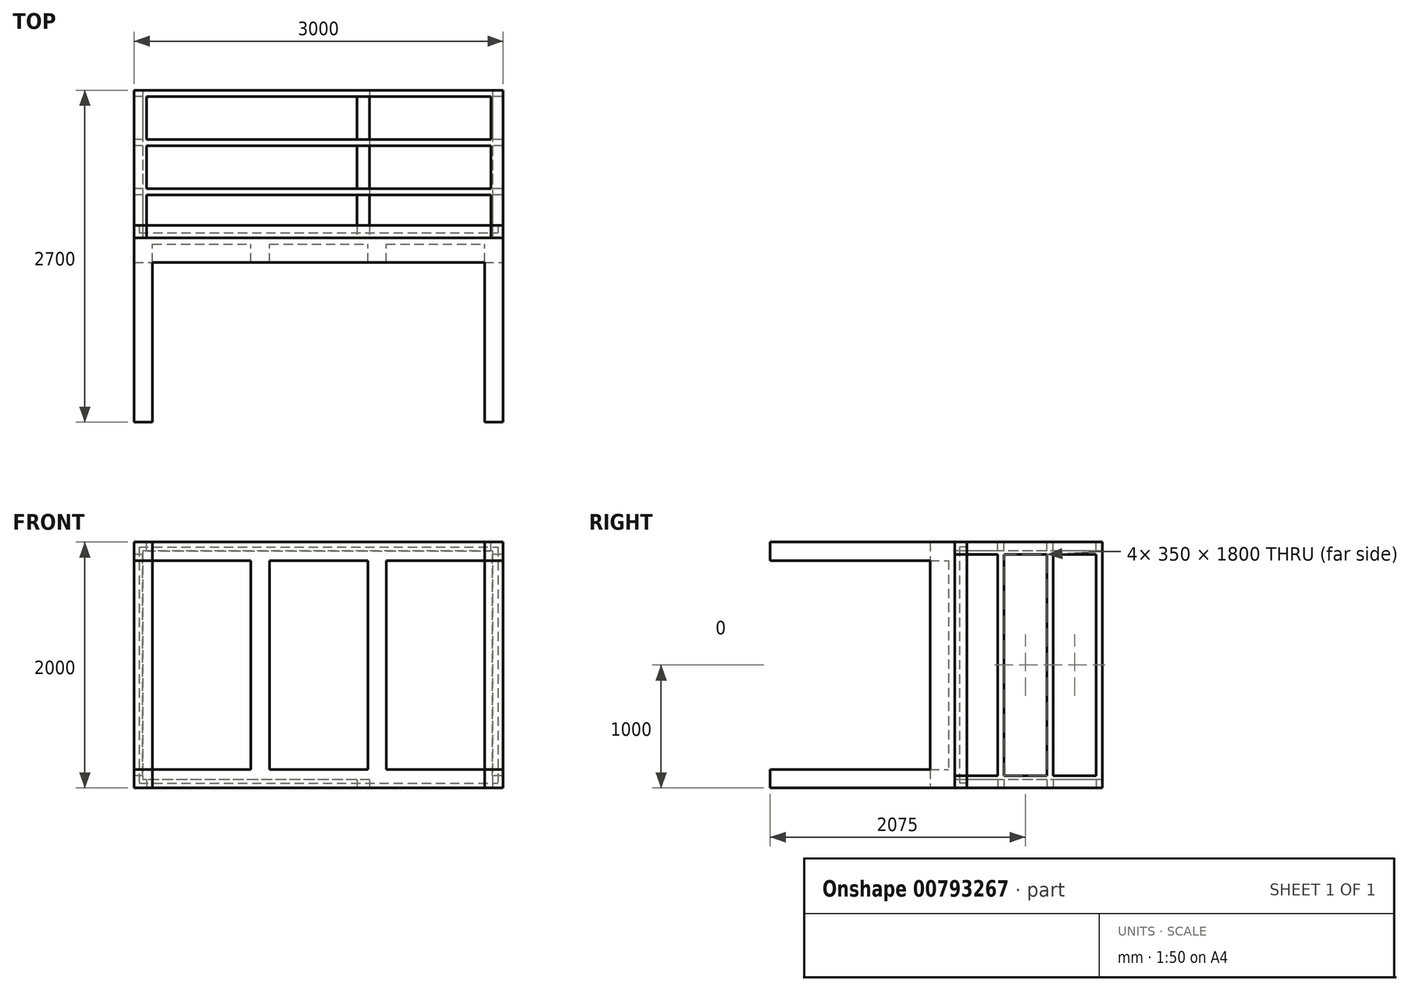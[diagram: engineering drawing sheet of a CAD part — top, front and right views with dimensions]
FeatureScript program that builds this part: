
annotation { "Feature Type Name" : "Feature", "Feature Type Description" : "" }
export const myFeature = defineFeature(function(context is Context, id is Id, definition is map)
    precondition{}
    {
        {
            var Q0;
            Q0=qCreatedBy(makeId("Front.planeOp"),FACE);
            var sketch = newSketch(context, id + "F0", { "sketchPlane" : qUnion([Q0])});
            skLineSegment(sketch, "E0.bottom", {"start": v(-1500, 1000) * mm, "end": v(1500, 1000) * mm});
            skLineSegment(sketch, "E0.top", {"start": v(-1500, -1000) * mm, "end": v(1500, -1000) * mm});
            skLineSegment(sketch, "E0.left", {"start": v(-1500, 1000) * mm, "end": v(-1500, -1000) * mm});
            skLineSegment(sketch, "E0.right", {"start": v(1500, 1000) * mm, "end": v(1500, -1000) * mm});
            skPoint(sketch, "E0.middle", {"position": v(0, 0) * mm});
            skSolve(sketch);
        }
        {
            var Q0;
            Q0=qSketchRegion(id+"F0",true);
            extrude(context, id + "F1", {"entities" : qUnion([Q0]), "depth" : 50 * mm, "offsetDistance" : 25 * mm});
        }
        {
            var Q0;
            Q0=makeQuery(id+"F1.opExtrude","CAP_FACE",FACE,{"disambiguationData":[OSD([sQuery(id+"F0.wireOp",EDGE,"E0.bottom"),sQuery(id+"F0.wireOp",EDGE,"E0.top"),sQuery(id+"F0.wireOp",EDGE,"E0.left"),sQuery(id+"F0.wireOp",EDGE,"E0.right")])],"isStart":false});
            var sketch = newSketch(context, id + "F2", { "sketchPlane" : qUnion([Q0])});
            skLineSegment(sketch, "E1.bottom", {"start": v(-1500, 1000) * mm, "end": v(-1350, 1000) * mm});
            skLineSegment(sketch, "E1.top", {"start": v(-1500, 850) * mm, "end": v(-1350, 850) * mm});
            skLineSegment(sketch, "E1.left", {"start": v(-1500, 1000) * mm, "end": v(-1500, 850) * mm});
            skLineSegment(sketch, "E1.right", {"start": v(-1350, 1000) * mm, "end": v(-1350, 850) * mm});
            skLineSegment(sketch, "E2.bottom", {"start": v(1350, 1000) * mm, "end": v(1500, 1000) * mm});
            skLineSegment(sketch, "E2.top", {"start": v(1350, 850) * mm, "end": v(1500, 850) * mm});
            skLineSegment(sketch, "E2.left", {"start": v(1350, 1000) * mm, "end": v(1350, 850) * mm});
            skLineSegment(sketch, "E2.right", {"start": v(1500, 1000) * mm, "end": v(1500, 850) * mm});
            skLineSegment(sketch, "E3.bottom", {"start": v(-1500, -850) * mm, "end": v(-1350, -850) * mm});
            skLineSegment(sketch, "E3.top", {"start": v(-1500, -1000) * mm, "end": v(-1350, -1000) * mm});
            skLineSegment(sketch, "E3.left", {"start": v(-1500, -850) * mm, "end": v(-1500, -1000) * mm});
            skLineSegment(sketch, "E3.right", {"start": v(-1350, -850) * mm, "end": v(-1350, -1000) * mm});
            skLineSegment(sketch, "E4.bottom", {"start": v(1500, -850) * mm, "end": v(1350, -850) * mm});
            skLineSegment(sketch, "E4.top", {"start": v(1500, -1000) * mm, "end": v(1350, -1000) * mm});
            skLineSegment(sketch, "E4.left", {"start": v(1500, -850) * mm, "end": v(1500, -1000) * mm});
            skLineSegment(sketch, "E4.right", {"start": v(1350, -850) * mm, "end": v(1350, -1000) * mm});
            skSolve(sketch);
        }
        {
            var Q0;
            Q0=qSketchRegion(id+"F2",true);
            extrude(context, id + "F3", {"entities" : qUnion([Q0]), "operationType" : NewBodyOperationType.ADD, "depth" : 1450 * mm, "offsetDistance" : 25 * mm});
        }
        {
            var Q0;
            Q0=makeQuery(id+"F1.opExtrude","CAP_FACE",FACE,{"disambiguationData":[OSD([sQuery(id+"F0.wireOp",EDGE,"E0.bottom"),sQuery(id+"F0.wireOp",EDGE,"E0.top"),sQuery(id+"F0.wireOp",EDGE,"E0.left"),sQuery(id+"F0.wireOp",EDGE,"E0.right")])],"isStart":true});
            var sketch = newSketch(context, id + "F4", { "sketchPlane" : qUnion([Q0])});
            skLineSegment(sketch, "E5", {"start": v(-1413.13, 927.5) * mm, "end": v(1430.62, 927.5) * mm});
            skLineSegment(sketch, "E6", {"start": v(-1413.13, 927.5) * mm, "end": v(-1413.13, -1000) * mm});
            skLineSegment(sketch, "E7", {"start": v(1430.62, 927.5) * mm, "end": v(1430.62, -933.33) * mm});
            skLineSegment(sketch, "E8", {"start": v(-413.13, -933.33) * mm, "end": v(-413.13, -1000) * mm});
            skLineSegment(sketch, "E9", {"start": v(-413.13, -933.33) * mm, "end": v(1430.62, -933.33) * mm});
            skPoint(sketch, "E10.orphan", {"position": v(1430.62, -1000) * mm});
            skSolve(sketch);
        }
        {
            var Q0;
            Q0=qSketchRegion(id+"F4",true);
            var Q1;
            Q1=makeQuery(id+"F4.imprint","IMPRINT",FACE,{"disambiguationData":[TD([[makeQuery(id+"F4.imprint","IMPRINT",EDGE,{"derivedFrom":sQuery(id+"F4.wireOp",EDGE,"E5")}),1.0]])]});
            extrude(context, id + "F5", {"entities" : qUnion([Q0, Q1]), "depth" : 1200 * mm, "offsetDistance" : 25 * mm});
        }
        {
            var Q0;
            Q0=makeQuery(id+"F5.opExtrude","SWEPT_FACE",FACE,{"disambiguationData":[OSD([sQuery(id+"F0.wireOp",EDGE,"E0.left")])]});
            var sketch = newSketch(context, id + "F6", { "sketchPlane" : qUnion([Q0])});
            skLineSegment(sketch, "E11", {"start": v(-1150, -900) * mm, "end": v(-1150, 900) * mm});
            skLineSegment(sketch, "E12", {"start": v(-800, -900) * mm, "end": v(-800, 900) * mm});
            skLineSegment(sketch, "E13", {"start": v(-750, -900) * mm, "end": v(-750, 900) * mm});
            skLineSegment(sketch, "E14", {"start": v(-400, -900) * mm, "end": v(-400, 900) * mm});
            skLineSegment(sketch, "E15", {"start": v(-350, -900) * mm, "end": v(-350, 900) * mm});
            skLineSegment(sketch, "E16", {"start": v(-1150, -900) * mm, "end": v(-800, -900) * mm});
            skLineSegment(sketch, "E17", {"start": v(-1150, 900) * mm, "end": v(-800, 900) * mm});
            skLineSegment(sketch, "E18.trimOffspring", {"start": v(-750, 900) * mm, "end": v(-400, 900) * mm});
            skLineSegment(sketch, "E19.trimOffspring", {"start": v(-350, 900) * mm, "end": v(0, 900) * mm});
            skLineSegment(sketch, "E20.trimOffspring", {"start": v(-350, -900) * mm, "end": v(0, -900) * mm});
            skLineSegment(sketch, "E21.trimOffspring", {"start": v(-750, -900) * mm, "end": v(-400, -900) * mm});
            skSolve(sketch);
        }
        {
            var Q0;
            Q0=makeQuery(id+"F6.imprint","IMPRINT",FACE,{"disambiguationData":[TD([[makeQuery(id+"F6.imprint","IMPRINT",EDGE,{"derivedFrom":sQuery(id+"F6.wireOp",EDGE,"E11")}),-1.0]])]});
            var Q1;
            Q1=makeQuery(id+"F6.imprint","IMPRINT",FACE,{"disambiguationData":[TD([[makeQuery(id+"F6.imprint","IMPRINT",EDGE,{"derivedFrom":sQuery(id+"F6.wireOp",EDGE,"E13")}),-1.0]])]});
            var Q2;
            Q2=makeQuery(id+"F6.imprint","IMPRINT",FACE,{"disambiguationData":[TD([[makeQuery(id+"F6.imprint","IMPRINT",EDGE,{"derivedFrom":sQuery(id+"F6.wireOp",EDGE,"E15")}),-1.0]])]});
            extrude(context, id + "F7", {"entities" : qUnion([Q0, Q1, Q2]), "operationType" : NewBodyOperationType.REMOVE, "endBound" : BoundingType.THROUGH_ALL, "oppositeDirection" : true, "depth" : 25 * mm, "offsetDistance" : 25 * mm});
        }
        {
            var Q0;
            {var subQ0=sQuery(id+"F0.wireOp",EDGE,"E0.top");var subQ1=makeQuery(id+"F1.opExtrude","CAP_EDGE",EDGE,{"disambiguationData":[OSD([subQ0])],"isStart":true});Q0=makeQuery(id+"F5.opExtrude","SWEPT_FACE",FACE,{"disambiguationData":[OSD([subQ0]),TDD([makeQuery(id+"F4.imprint","IMPRINT",EDGE,{"disambiguationData":[TD([[makeQuery(id+"F4.imprint","INTERSECT",VERTEX,{"derivedFrom":[subQ1,makeQuery(id+"F1.opExtrude","CAP_EDGE",EDGE,{"disambiguationData":[OSD([sQuery(id+"F0.wireOp",EDGE,"E0.left")])],"isStart":true})]}),-1.0]])],"derivedFrom":subQ1})])]});}
            var sketch = newSketch(context, id + "F8", { "sketchPlane" : qUnion([Q0])});
            skLineSegment(sketch, "E22", {"start": v(313.13, 0) * mm, "end": v(313.13, -350) * mm});
            skLineSegment(sketch, "E23", {"start": v(-1400, -350) * mm, "end": v(313.13, -350) * mm});
            skLineSegment(sketch, "E24", {"start": v(-1400, -400) * mm, "end": v(313.13, -400) * mm});
            skLineSegment(sketch, "E25", {"start": v(-1400, -750) * mm, "end": v(313.13, -750) * mm});
            skLineSegment(sketch, "E26", {"start": v(-1400, -800) * mm, "end": v(313.13, -800) * mm});
            skLineSegment(sketch, "E27", {"start": v(-1400, -1150) * mm, "end": v(313.13, -1150) * mm});
            skLineSegment(sketch, "E28.trimOffspring", {"start": v(313.13, -400) * mm, "end": v(313.13, -750) * mm});
            skLineSegment(sketch, "E29.trimOffspring", {"start": v(313.13, -800) * mm, "end": v(313.13, -1150) * mm});
            skLineSegment(sketch, "E30", {"start": v(-1400, 0) * mm, "end": v(-1400, -350) * mm});
            skLineSegment(sketch, "E31.trimOffspring", {"start": v(-1400, -400) * mm, "end": v(-1400, -750) * mm});
            skLineSegment(sketch, "E32.trimOffspring", {"start": v(-1400, -800) * mm, "end": v(-1400, -1150) * mm});
            skSolve(sketch);
        }
        {
            var Q0;
            Q0=makeQuery(id+"F8.imprint","IMPRINT",FACE,{"disambiguationData":[TD([[makeQuery(id+"F8.imprint","IMPRINT",EDGE,{"derivedFrom":sQuery(id+"F8.wireOp",EDGE,"E26")}),-1.0]])]});
            var Q1;
            {var subQ0=sQuery(id+"F8.wireOp",EDGE,"E22");Q1=makeQuery(id+"F8.imprint","IMPRINT",FACE,{"disambiguationData":[TD([[makeQuery(id+"F8.imprint","IMPRINT",EDGE,{"derivedFrom":subQ0}),-1.0]])]});}
            var Q2;
            Q2=makeQuery(id+"F8.imprint","IMPRINT",FACE,{"disambiguationData":[TD([[makeQuery(id+"F8.imprint","IMPRINT",EDGE,{"derivedFrom":sQuery(id+"F8.wireOp",EDGE,"E24")}),-1.0]])]});
            extrude(context, id + "F9", {"entities" : qUnion([Q0, Q1, Q2]), "operationType" : NewBodyOperationType.REMOVE, "oppositeDirection" : true, "depth" : 110 * mm, "offsetDistance" : 25 * mm});
        }
        {
            var Q0;
            Q0=makeQuery(id+"F5.opExtrude","SWEPT_FACE",FACE,{"disambiguationData":[OSD([sQuery(id+"F0.wireOp",EDGE,"E0.bottom")])]});
            var sketch = newSketch(context, id + "F10", { "sketchPlane" : qUnion([Q0])});
            skLineSegment(sketch, "E33", {"start": v(-1400, 1150) * mm, "end": v(-1400, 800) * mm});
            skLineSegment(sketch, "E34", {"start": v(1400, 1150) * mm, "end": v(1400, 800) * mm});
            skLineSegment(sketch, "E35", {"start": v(-1400, 1150) * mm, "end": v(1400, 1150) * mm});
            skLineSegment(sketch, "E36", {"start": v(-1400, 800) * mm, "end": v(1400, 800) * mm});
            skLineSegment(sketch, "E37", {"start": v(-1400, 750) * mm, "end": v(1400, 750) * mm});
            skLineSegment(sketch, "E38", {"start": v(-1400, 400) * mm, "end": v(1400, 400) * mm});
            skLineSegment(sketch, "E39", {"start": v(1400, 350) * mm, "end": v(-1400, 350) * mm});
            skLineSegment(sketch, "E40.trimOffspring", {"start": v(1400, 750) * mm, "end": v(1400, 400) * mm});
            skLineSegment(sketch, "E41.trimOffspring", {"start": v(1400, 350) * mm, "end": v(1400, 0) * mm});
            skLineSegment(sketch, "E42.trimOffspring", {"start": v(-1400, 350) * mm, "end": v(-1400, 0) * mm});
            skLineSegment(sketch, "E43.trimOffspring", {"start": v(-1400, 750) * mm, "end": v(-1400, 400) * mm});
            skSolve(sketch);
        }
        {
            var Q0;
            Q0=makeQuery(id+"F10.imprint","IMPRINT",FACE,{"disambiguationData":[TD([[makeQuery(id+"F10.imprint","IMPRINT",EDGE,{"derivedFrom":sQuery(id+"F10.wireOp",EDGE,"E33")}),1.0]])]});
            var Q1;
            Q1=makeQuery(id+"F10.imprint","IMPRINT",FACE,{"disambiguationData":[TD([[makeQuery(id+"F10.imprint","IMPRINT",EDGE,{"derivedFrom":sQuery(id+"F10.wireOp",EDGE,"E37")}),-1.0]])]});
            var Q2;
            Q2=makeQuery(id+"F10.imprint","IMPRINT",FACE,{"disambiguationData":[TD([[makeQuery(id+"F10.imprint","IMPRINT",EDGE,{"derivedFrom":sQuery(id+"F10.wireOp",EDGE,"E39")}),1.0]])]});
            extrude(context, id + "F11", {"entities" : qUnion([Q0, Q1, Q2]), "operationType" : NewBodyOperationType.REMOVE, "oppositeDirection" : true, "depth" : 110 * mm, "offsetDistance" : 25 * mm});
        }
        {
            var Q0;
            Q0=makeQuery(id+"F1.opExtrude","CAP_FACE",FACE,{"disambiguationData":[OSD([sQuery(id+"F0.wireOp",EDGE,"E0.bottom"),sQuery(id+"F0.wireOp",EDGE,"E0.top"),sQuery(id+"F0.wireOp",EDGE,"E0.left"),sQuery(id+"F0.wireOp",EDGE,"E0.right")])],"isStart":true});
            extrude(context, id + "F12", {"entities" : qUnion([Q0]), "depth" : 100 * mm, "offsetDistance" : 25 * mm});
        }
        {
            var Q0;
            Q0=makeQuery(id+"F1.opExtrude","CAP_FACE",FACE,{"disambiguationData":[OSD([sQuery(id+"F0.wireOp",EDGE,"E0.bottom"),sQuery(id+"F0.wireOp",EDGE,"E0.top"),sQuery(id+"F0.wireOp",EDGE,"E0.left"),sQuery(id+"F0.wireOp",EDGE,"E0.right")])],"isStart":false});
            var sketch = newSketch(context, id + "F13", { "sketchPlane" : qUnion([Q0])});
            skLineSegment(sketch, "E44", {"start": v(-1350, 850) * mm, "end": v(-1350, -850) * mm});
            skLineSegment(sketch, "E45", {"start": v(1350, 850) * mm, "end": v(1350, -850) * mm});
            skLineSegment(sketch, "E46", {"start": v(-1350, 850) * mm, "end": v(1350, 850) * mm});
            skLineSegment(sketch, "E47", {"start": v(-1350, -850) * mm, "end": v(1350, -850) * mm});
            skSolve(sketch);
        }
        {
            var Q0;
            Q0=makeQuery(id+"F13.imprint","IMPRINT",FACE,{"disambiguationData":[TD([[makeQuery(id+"F13.imprint","IMPRINT",EDGE,{"derivedFrom":sQuery(id+"F13.wireOp",EDGE,"E44")}),-1.0]])]});
            var Q1;
            Q1=makeQuery(id+"F13.imprint","IMPRINT",FACE,{"disambiguationData":[TD([[makeQuery(id+"F13.imprint","IMPRINT",EDGE,{"derivedFrom":sQuery(id+"F13.wireOp",EDGE,"E46")}),1.0]])]});
            var Q2;
            Q2=makeQuery(id+"F13.imprint","IMPRINT",FACE,{"disambiguationData":[TD([[makeQuery(id+"F13.imprint","IMPRINT",EDGE,{"derivedFrom":sQuery(id+"F13.wireOp",EDGE,"E45")}),1.0]])]});
            var Q3;
            Q3=makeQuery(id+"F13.imprint","IMPRINT",FACE,{"disambiguationData":[TD([[makeQuery(id+"F13.imprint","IMPRINT",EDGE,{"derivedFrom":sQuery(id+"F13.wireOp",EDGE,"E47")}),-1.0]])]});
            extrude(context, id + "F14", {"entities" : qUnion([Q0, Q1, Q2, Q3]), "operationType" : NewBodyOperationType.ADD, "depth" : 150 * mm, "offsetDistance" : 25 * mm});
        }
        {
            var Q0;
            Q0=makeQuery(id+"F1.opExtrude","CAP_FACE",FACE,{"disambiguationData":[OSD([sQuery(id+"F0.wireOp",EDGE,"E0.bottom"),sQuery(id+"F0.wireOp",EDGE,"E0.top"),sQuery(id+"F0.wireOp",EDGE,"E0.left"),sQuery(id+"F0.wireOp",EDGE,"E0.right")])],"isStart":false});
            var sketch = newSketch(context, id + "F15", { "sketchPlane" : qUnion([Q0])});
            skLineSegment(sketch, "E48.bottom", {"start": v(-550, 850) * mm, "end": v(-400, 850) * mm});
            skLineSegment(sketch, "E48.top", {"start": v(-550, -850) * mm, "end": v(-400, -850) * mm});
            skLineSegment(sketch, "E48.left", {"start": v(-550, 850) * mm, "end": v(-550, -850) * mm});
            skLineSegment(sketch, "E48.right", {"start": v(-400, 850) * mm, "end": v(-400, -850) * mm});
            skLineSegment(sketch, "E49.bottom", {"start": v(400, 850) * mm, "end": v(550, 850) * mm});
            skLineSegment(sketch, "E49.top", {"start": v(400, -850) * mm, "end": v(550, -850) * mm});
            skLineSegment(sketch, "E49.left", {"start": v(400, 850) * mm, "end": v(400, -850) * mm});
            skLineSegment(sketch, "E49.right", {"start": v(550, 850) * mm, "end": v(550, -850) * mm});
            skSolve(sketch);
        }
        {
            var Q0;
            Q0=makeQuery(id+"F15.imprint","IMPRINT",FACE,{"disambiguationData":[TD([[makeQuery(id+"F15.imprint","IMPRINT",EDGE,{"derivedFrom":sQuery(id+"F15.wireOp",EDGE,"E48.bottom")}),-1.0]])]});
            var Q1;
            Q1=makeQuery(id+"F15.imprint","IMPRINT",FACE,{"disambiguationData":[TD([[makeQuery(id+"F15.imprint","IMPRINT",EDGE,{"derivedFrom":sQuery(id+"F15.wireOp",EDGE,"E49.bottom")}),-1.0]])]});
            extrude(context, id + "F16", {"entities" : qUnion([Q0, Q1]), "operationType" : NewBodyOperationType.ADD, "depth" : 150 * mm, "offsetDistance" : 25 * mm});
        }
        {
            var Q0;
            Q0=makeQuery(id+"F12.opExtrude","CAP_FACE",FACE,{"disambiguationData":[OSD([sQuery(id+"F0.wireOp",EDGE,"E0.bottom"),sQuery(id+"F0.wireOp",EDGE,"E0.top"),sQuery(id+"F0.wireOp",EDGE,"E0.left"),sQuery(id+"F0.wireOp",EDGE,"E0.right")])],"isStart":false});
            shell(context, id + "F17", {"entities" : qUnion([Q0]), "thickness" : 40 * mm});
        }
    });
